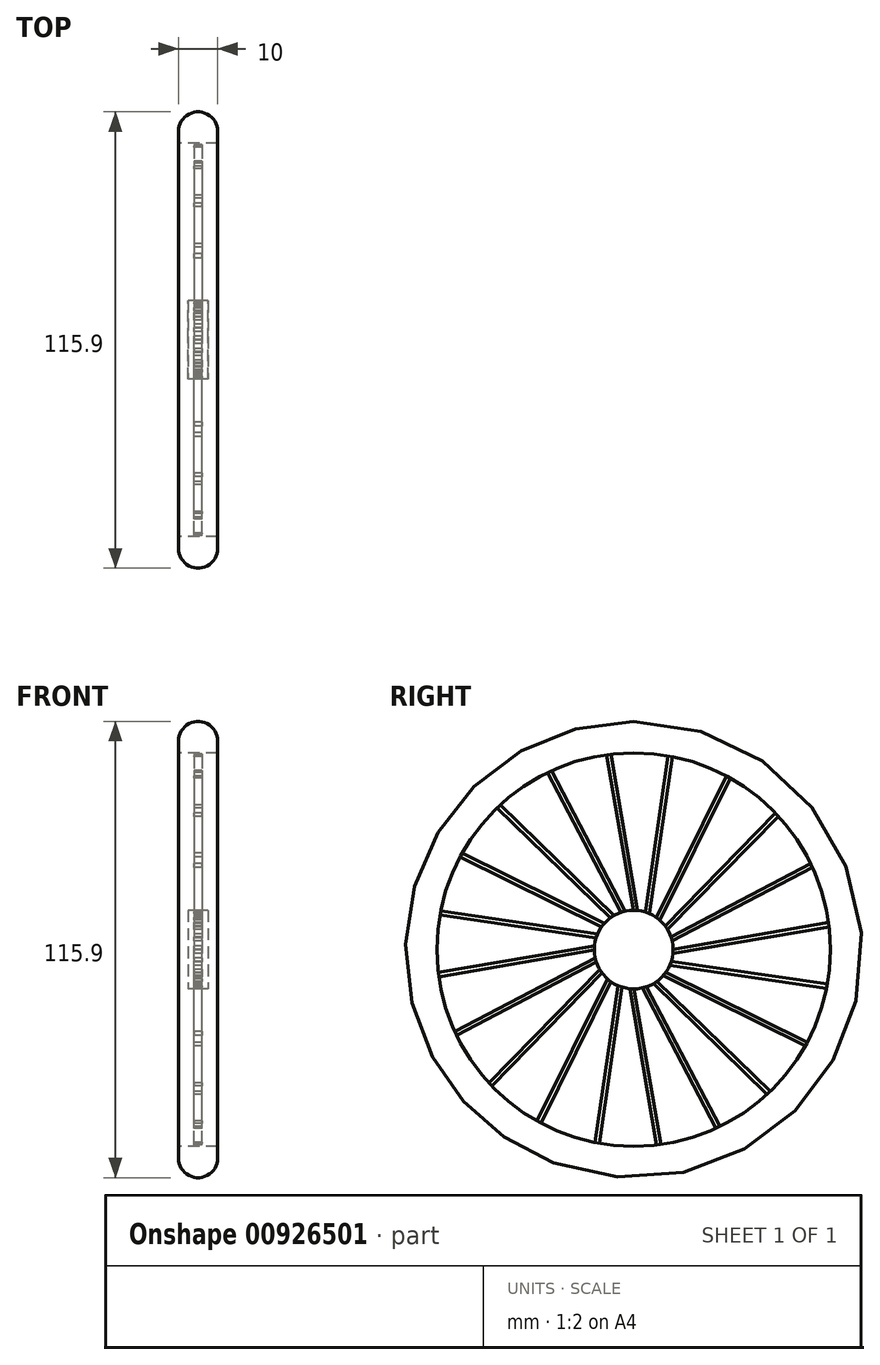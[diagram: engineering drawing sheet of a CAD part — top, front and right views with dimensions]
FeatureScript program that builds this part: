
annotation { "Feature Type Name" : "Feature", "Feature Type Description" : "" }
export const myFeature = defineFeature(function(context is Context, id is Id, definition is map)
    precondition{}
    {
        {
            var Q0;
            Q0=qCreatedBy(makeId("Front.planeOp"),FACE);
            var sketch = newSketch(context, id + "F0", { "sketchPlane" : qUnion([Q0])});
            skArc(sketch, "E0", {"start": v(5, 52.95) * mm, "mid": v(0, 57.95) * mm, "end": v(-5, 52.95) * mm});
            skLineSegment(sketch, "E1", {"start": v(-5, 52.95) * mm, "end": v(-5, 50) * mm});
            skLineSegment(sketch, "E2", {"start": v(-5, 50) * mm, "end": v(5, 50) * mm});
            skLineSegment(sketch, "E3", {"start": v(5, 50) * mm, "end": v(5, 52.95) * mm});
            skLineSegment(sketch, "E4.bottom", {"start": v(-2.5, 10) * mm, "end": v(2.5, 10) * mm});
            skLineSegment(sketch, "E4.top", {"start": v(-2.5, 0) * mm, "end": v(2.5, 0) * mm});
            skLineSegment(sketch, "E4.left", {"start": v(-2.5, 10) * mm, "end": v(-2.5, 0) * mm});
            skLineSegment(sketch, "E4.right", {"start": v(2.5, 10) * mm, "end": v(2.5, 0) * mm});
            skLineSegment(sketch, "E5", {"start": v(-18.34, 0) * mm, "end": v(15.51, 0) * mm});
            skSolve(sketch);
        }
        {
            var Q0;
            Q0=makeQuery(id+"F0.imprint","IMPRINT",FACE,{"disambiguationData":[TD([[makeQuery(id+"F0.imprint","IMPRINT",EDGE,{"derivedFrom":sQuery(id+"F0.wireOp",EDGE,"E0")}),1.0]])]});
            var Q1;
            Q1=makeQuery(id+"F0.imprint","IMPRINT",FACE,{"disambiguationData":[TD([[makeQuery(id+"F0.imprint","IMPRINT",EDGE,{"derivedFrom":sQuery(id+"F0.wireOp",EDGE,"E4.bottom")}),-1.0]])]});
            var Q2;
            Q2=sQuery(id+"F0.wireOp",EDGE,"E5");
            revolve(context, id + "F1", {"surfaceOperationType" : NewSurfaceOperationType.NEW, "entities" : qUnion([Q0, Q1]), "axis" : qUnion([Q2]), "revolveType" : RevolveType.FULL});
        }
        {
            var Q0;
            Q0=makeQuery(id+"F1.opRevolve","SWEPT_FACE",FACE,{"disambiguationData":[OSD([sQuery(id+"F0.wireOp",EDGE,"E1")])]});
            var sketch = newSketch(context, id + "F2", { "sketchPlane" : qUnion([Q0])});
            skCircle(sketch, "E6", {"center": v(-46.64, 21.49) * mm, "radius": 0.5 * mm});
            skSolve(sketch);
        }
        {
            var Q0;
            Q0=makeQuery(id+"F2.imprint","IMPRINT",FACE,{"disambiguationData":[TD([[makeQuery(id+"F2.imprint","IMPRINT",EDGE,{"derivedFrom":sQuery(id+"F2.wireOp",EDGE,"E6")}),1.0]])]});
            var Q1;
            Q1=sQuery(id+"F2.wireOp",EDGE,"E6");
            extrude(context, id + "F3", {"entities" : qUnion([Q0]), "operationType" : NewBodyOperationType.REMOVE, "surfaceEntities" : qUnion([Q1]), "oppositeDirection" : true, "depth" : 59.6 * mm, "offsetDistance" : 25 * mm});
        }
        {
            var Q0;
            Q0=makeQuery(id+"F1.opRevolve","SWEPT_BODY",BODY,{"disambiguationData":[OSD([sQuery(id+"F0.wireOp",EDGE,"E0"),sQuery(id+"F0.wireOp",EDGE,"E1"),sQuery(id+"F0.wireOp",EDGE,"E2"),sQuery(id+"F0.wireOp",EDGE,"E3")])]});
            var Q1;
            Q1=makeQuery(id+"F1.opRevolve","SWEPT_EDGE",EDGE,{"disambiguationData":[OSD([sQuery(id+"F0.wireOp",EDGE,"E1"),sQuery(id+"F0.wireOp",EDGE,"E2")])]});
            circularPattern(context, id + "F4", {"entities" : qUnion([Q0]), "axis" : qUnion([Q1]), "angle" : 360 * degree, "instanceCount" : 20, "equalSpace" : true});
        }
        {
            var Q0;
            Q0=qCreatedBy(makeId("Right.planeOp"),FACE);
            var sketch = newSketch(context, id + "F5", { "sketchPlane" : qUnion([Q0])});
            skLineSegment(sketch, "E7", {"start": v(37.7, 34.8) * mm, "end": v(7.35, 3.78) * mm});
            skLineSegment(sketch, "E8", {"start": v(7.35, 3.78) * mm, "end": v(6.62, 4.5) * mm});
            skLineSegment(sketch, "E9", {"start": v(37.7, 34.8) * mm, "end": v(36.88, 35.59) * mm});
            skLineSegment(sketch, "E10", {"start": v(36.88, 35.59) * mm, "end": v(6.62, 4.5) * mm});
            skSolve(sketch);
        }
        {
            var Q0;
            Q0=makeQuery(id+"F5.imprint","IMPRINT",FACE,{"disambiguationData":[TD([[makeQuery(id+"F5.imprint","IMPRINT",EDGE,{"derivedFrom":sQuery(id+"F5.wireOp",EDGE,"E7")}),-1.0]])]});
            extrude(context, id + "F6", {"entities" : qUnion([Q0]), "endBound" : BoundingType.SYMMETRIC, "depth" : 2 * mm, "offsetDistance" : 25 * mm});
        }
        {
            var Q0;
            Q0=makeQuery(id+"F6.opExtrude","SWEPT_BODY",BODY,{"disambiguationData":[OSD([sQuery(id+"F5.wireOp",EDGE,"E7"),sQuery(id+"F5.wireOp",EDGE,"E8"),sQuery(id+"F5.wireOp",EDGE,"E9"),sQuery(id+"F5.wireOp",EDGE,"E10")])]});
            var Q1;
            Q1=makeQuery(id+"F4.opPattern","COPY",EDGE,{"derivedFrom":makeQuery(id+"F1.opRevolve","SWEPT_EDGE",EDGE,{"disambiguationData":[OSD([sQuery(id+"F0.wireOp",EDGE,"E2"),sQuery(id+"F0.wireOp",EDGE,"E3")])]}),"instanceName":"9"});
            circularPattern(context, id + "F7", {"operationType" : NewBodyOperationType.ADD, "entities" : qUnion([Q0]), "axis" : qUnion([Q1]), "angle" : 360 * degree, "instanceCount" : 20, "equalSpace" : true});
        }
    });
